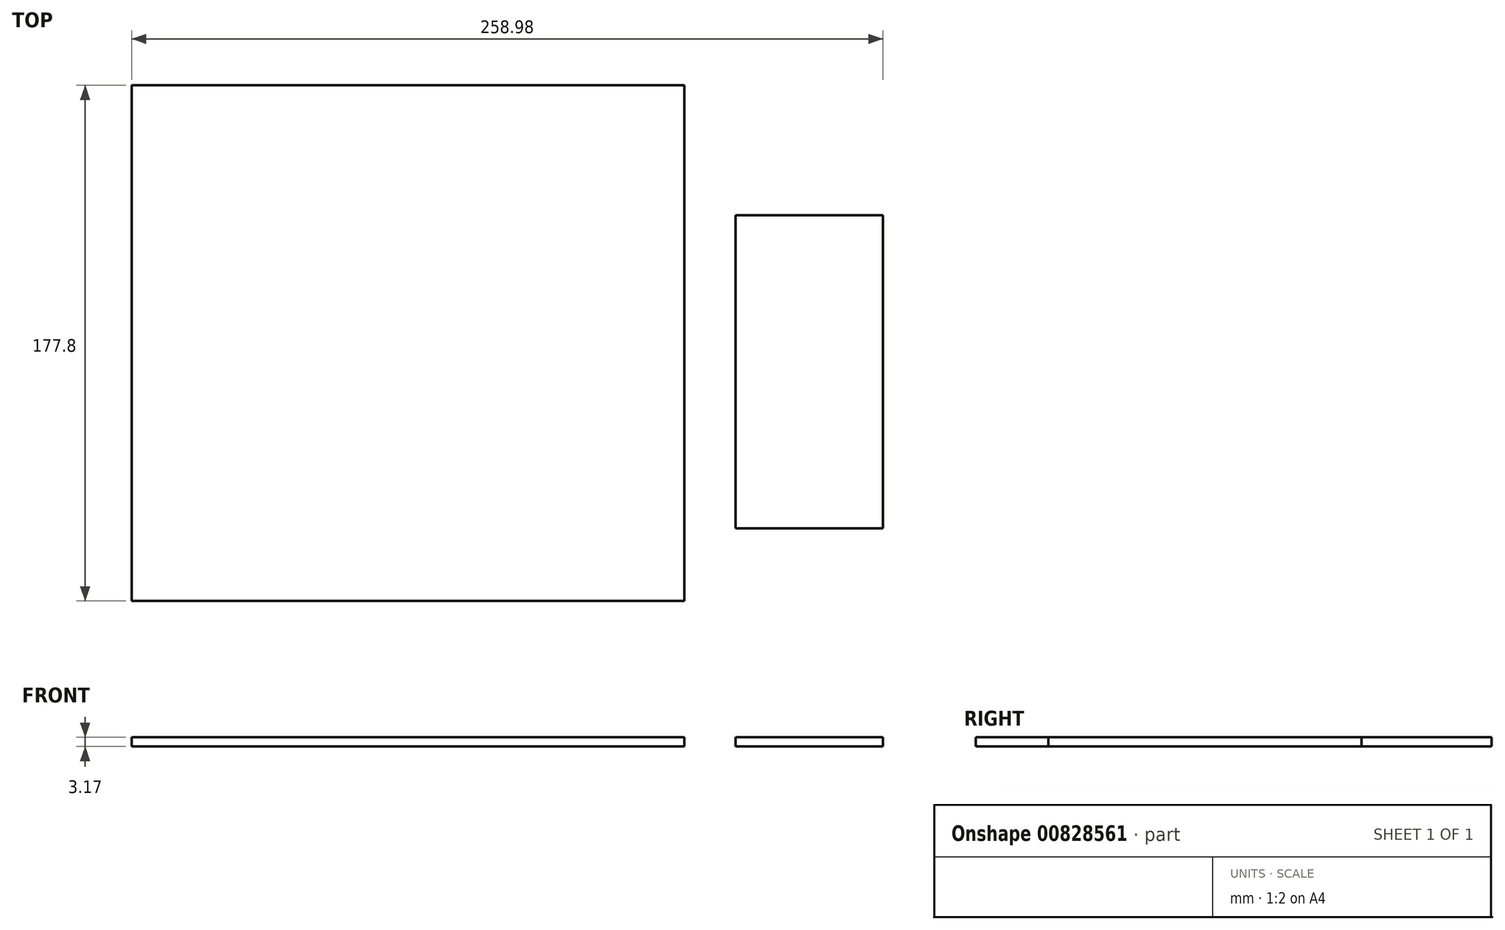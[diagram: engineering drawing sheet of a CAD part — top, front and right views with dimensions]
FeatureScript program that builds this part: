
annotation { "Feature Type Name" : "Feature", "Feature Type Description" : "" }
export const myFeature = defineFeature(function(context is Context, id is Id, definition is map)
    precondition{}
    {
        {
            var Q0;
            Q0=qCreatedBy(makeId("Top.planeOp"),FACE);
            var sketch = newSketch(context, id + "F0", { "sketchPlane" : qUnion([Q0])});
            skLineSegment(sketch, "E0.bottom", {"start": v(-104.7, 44.79) * mm, "end": v(85.8, 44.79) * mm});
            skLineSegment(sketch, "E0.top", {"start": v(-104.7, -133.01) * mm, "end": v(85.8, -133.01) * mm});
            skLineSegment(sketch, "E0.left", {"start": v(-104.7, 44.79) * mm, "end": v(-104.7, -133.01) * mm});
            skLineSegment(sketch, "E0.right", {"start": v(85.8, 44.79) * mm, "end": v(85.8, -133.01) * mm});
            skLineSegment(sketch, "E1.bottom", {"start": v(103.47, 0) * mm, "end": v(154.27, 0) * mm});
            skLineSegment(sketch, "E1.top", {"start": v(103.47, -107.95) * mm, "end": v(154.27, -107.95) * mm});
            skLineSegment(sketch, "E1.left", {"start": v(103.47, 0) * mm, "end": v(103.47, -107.95) * mm});
            skLineSegment(sketch, "E1.right", {"start": v(154.27, 0) * mm, "end": v(154.27, -107.95) * mm});
            skSolve(sketch);
        }
        {
            var Q0;
            Q0=makeQuery(id+"F0.imprint","IMPRINT",FACE,{"disambiguationData":[TD([[makeQuery(id+"F0.imprint","IMPRINT",EDGE,{"derivedFrom":sQuery(id+"F0.wireOp",EDGE,"E0.bottom")}),-1.0]])]});
            var Q1;
            Q1=makeQuery(id+"F0.imprint","IMPRINT",FACE,{"disambiguationData":[TD([[makeQuery(id+"F0.imprint","IMPRINT",EDGE,{"derivedFrom":sQuery(id+"F0.wireOp",EDGE,"E1.bottom")}),-1.0]])]});
            extrude(context, id + "F1", {"entities" : qUnion([Q0, Q1]), "depth" : 3.17 * mm, "offsetDistance" : 25.4 * mm});
        }
    });
